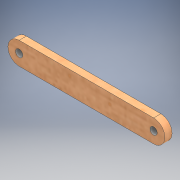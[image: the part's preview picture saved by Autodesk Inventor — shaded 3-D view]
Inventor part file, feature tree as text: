
AUTODESK INVENTOR PART (.ipt)
format: ipt  version: 2018 (Build 220112000, 112)  size: 116,736 bytes
history: native  units: mm
features: extrude x1, sketch x1
ambient origin geometry x8: Origin, YZ Plane, XZ Plane, XY Plane, X Axis, Y Axis, Z Axis, Center Point
bodies: Solid1 (feature_tree)
feature tree (2):
  extrude  "Extrusion1"  Depth=3.2mm
  sketch  "Sketch1"  dims[d0=3.2mm d1=3.2mm d2=59.756mm d3=5.0mm d4=5.0mm d5=3.2mm d6=0.0mm]
